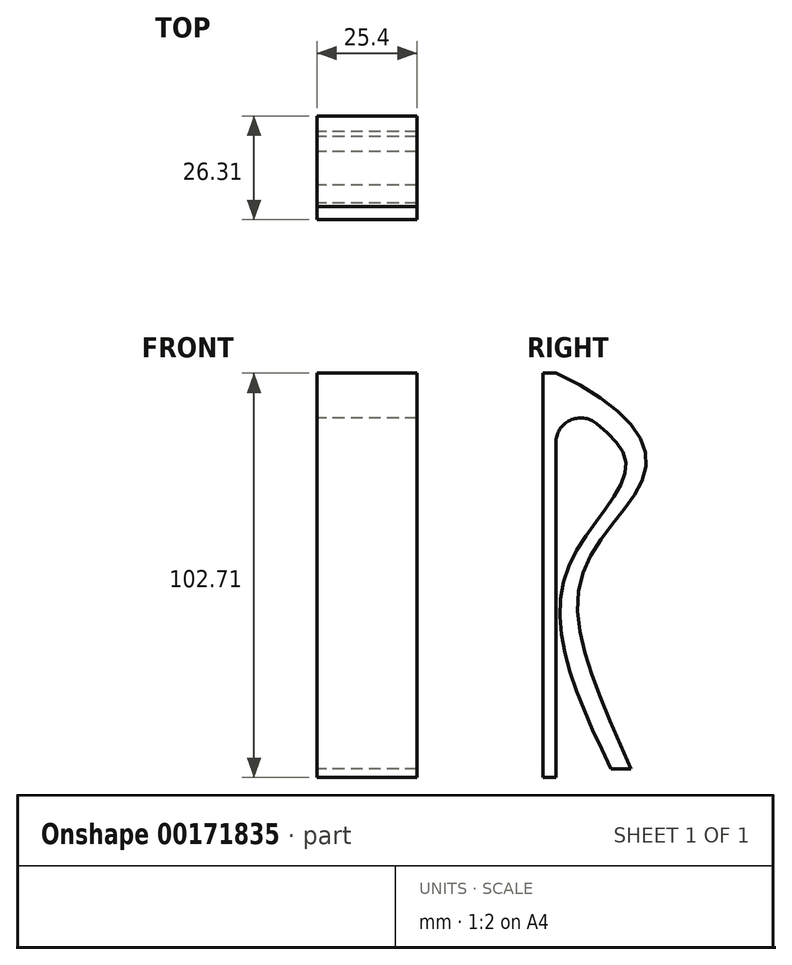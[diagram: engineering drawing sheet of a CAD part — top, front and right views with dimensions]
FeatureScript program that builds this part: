
annotation { "Feature Type Name" : "Feature", "Feature Type Description" : "" }
export const myFeature = defineFeature(function(context is Context, id is Id, definition is map)
    precondition{}
    {
        {
            var Q0;
            Q0=qCreatedBy(makeId("Right.planeOp"),FACE);
            var sketch = newSketch(context, id + "F0", { "sketchPlane" : qUnion([Q0])});
            skFitSpline(sketch, "E0", {"points": [v(0, 46.43) * mm, v(17.85, 27.94) * mm, v(2.34, 0) * mm, v(14.04, -49) * mm], "startDerivative": vector(91.66, -69.44) * mm, "endDerivative": vector(62.33, -129.12) * mm});
            skLineSegment(sketch, "E1", {"start": v(14.04, -49) * mm, "end": v(19.07, -49) * mm});
            skFitSpline(sketch, "E2", {"points": [v(19.07, -49) * mm, v(6.59, 0) * mm, v(22.85, 27.14) * mm, v(0, 51.56) * mm], "startDerivative": vector(-60.46, 142.01) * mm, "endDerivative": vector(-148.96, 68.27) * mm});
            skLineSegment(sketch, "E3.bottom", {"start": v(0, 51.56) * mm, "end": v(-3.28, 51.56) * mm});
            skLineSegment(sketch, "E3.top", {"start": v(0, -51.15) * mm, "end": v(-3.28, -51.15) * mm});
            skLineSegment(sketch, "E3.left", {"start": v(0, 33.84) * mm, "end": v(0, -51.15) * mm});
            skLineSegment(sketch, "E3.right", {"start": v(-3.28, 51.56) * mm, "end": v(-3.28, -51.15) * mm});
            skArc(sketch, "E4.filletArc", {"start": v(10.3, 38.8) * mm, "mid": v(3.6, 39.56) * mm, "end": v(0, 33.84) * mm});
            skSolve(sketch);
        }
        {
            var Q0;
            Q0=makeQuery(id+"F0.imprint","IMPRINT",FACE,{"disambiguationData":[TD([[makeQuery(id+"F0.imprint","IMPRINT",EDGE,{"derivedFrom":sQuery(id+"F0.wireOp",EDGE,"E0")}),1.0]])]});
            var Q1;
            Q1=sQuery(id+"F0.wireOp",EDGE,"E0");
            extrude(context, id + "F1", {"entities" : qUnion([Q0]), "surfaceEntities" : qUnion([Q1]), "endBound" : BoundingType.SYMMETRIC, "depth" : 25.4 * mm});
        }
    });
